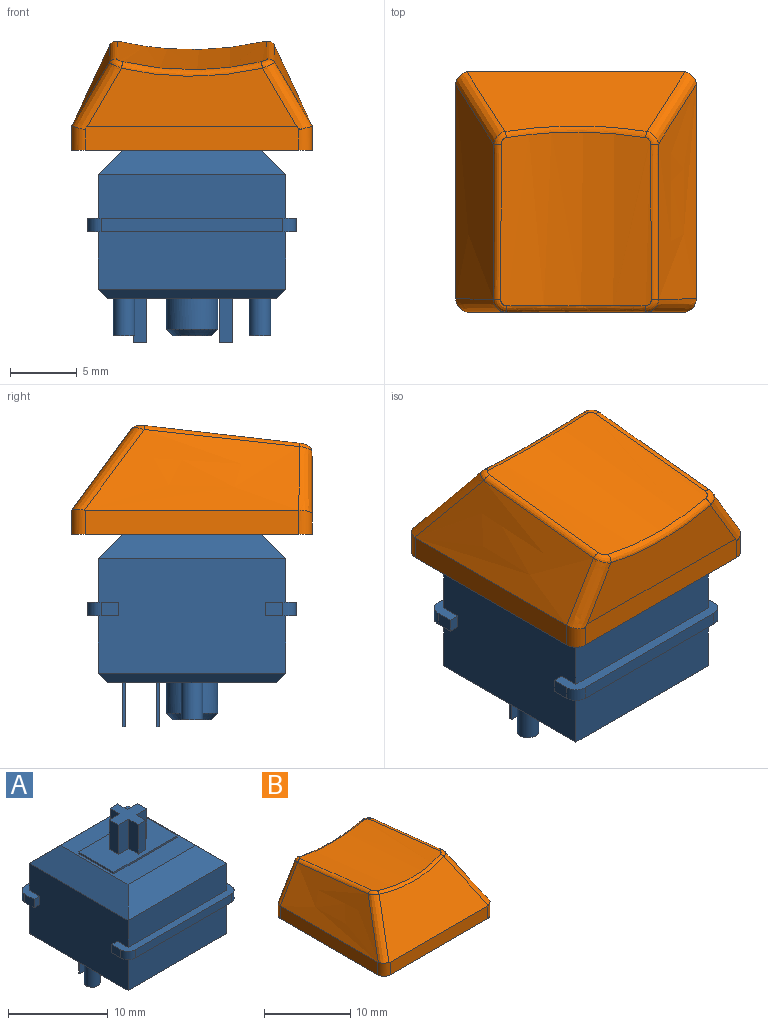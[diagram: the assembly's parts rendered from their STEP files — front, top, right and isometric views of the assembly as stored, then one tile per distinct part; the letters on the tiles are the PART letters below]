
ASSEMBLY  parts=2 mates=1
PART A: 69 faces, bbox 15.6x15.6x18.6 mm
  f0: plane 15.6x2.3mm, normal (0,0,-1), area 14.4mm2, adj f2,f3,f28,f30,f35,f60,f62,f63
  f1: plane 15.6x2.3mm, normal (0,0,-1), area 14.4mm2, adj f28,f30,f33,f34,f36,f59,f61,f64
  f2: plane 1.3x1mm, normal (1,0,0), area 1.3mm2, adj f0,f32,f62,f66
  f3: plane 1.3x1mm, normal (-1,0,0), area 1.3mm2, adj f0,f32,f63,f68
  f4: plane 15.6x2.3mm, normal (0,0,1), area 14.4mm2, adj f28,f30,f31,f33,f34,f36,f61,f64
  f5: plane 14x2.2mm, normal (-0.71,0,0.71), area 36.7mm2, adj f6,f7,f26,f30
  f6: plane 14x2.2mm, normal (0,-0.71,0.71), area 36.7mm2, adj f5,f7,f27,f31
  f7: plane 9.6x9.6mm, normal (0,0,1), area 47.2mm2, adj f5,f6,f8,f9,f10,f11,f26,f27
  f8: plane 5x0.2mm, normal (1,0,0), area 1mm2, adj f7,f9,f11,f12
  f9: plane 9x0.2mm, normal (0,1,0), area 1.8mm2, adj f7,f8,f10,f12
  f10: plane 5x0.2mm, normal (-1,0,0), area 1mm2, adj f7,f9,f11,f12
  f11: plane 9x0.2mm, normal (0,-1,0), area 1.8mm2, adj f7,f8,f10,f12
  f12: plane 9x5mm, normal (0,0,1), area 36.9mm2, adj f8,f9,f10,f11,f13,f14,f15,f16
  f13: plane 3.6x1.35mm, normal (1,0,0), area 4.9mm2, adj f12,f14,f24,f25
  f14: plane 3.6x1.08mm, normal (0,1,0), area 3.9mm2, adj f12,f13,f15,f25
  f15: plane 3.6x1.35mm, normal (-1,0,0), area 4.9mm2, adj f12,f14,f16,f25
  f16: plane 3.6x1.46mm, normal (0,1,0), area 5.3mm2, adj f12,f15,f17,f25
  f17: plane 3.6x1.3mm, normal (-1,0,0), area 4.7mm2, adj f12,f16,f18,f25
  f18: plane 3.6x1.46mm, normal (0,-1,0), area 5.3mm2, adj f12,f17,f19,f25
  f19: plane 3.6x1.35mm, normal (-1,0,0), area 4.9mm2, adj f12,f18,f20,f25
  f20: plane 3.6x1.08mm, normal (0,-1,0), area 3.9mm2, adj f12,f19,f21,f25
  f21: plane 3.6x1.35mm, normal (1,0,0), area 4.9mm2, adj f12,f20,f22,f25
  f22: plane 3.6x1.46mm, normal (0,-1,0), area 5.3mm2, adj f12,f21,f23,f25
  f23: plane 3.6x1.3mm, normal (1,0,0), area 4.7mm2, adj f12,f22,f24,f25
  f24: plane 3.6x1.46mm, normal (0,1,0), area 5.3mm2, adj f12,f13,f23,f25
  f25: plane 4x4mm, normal (0,0,1), area 8.1mm2, adj f13,f14,f15,f16,f17,f18,f19,f20
  f26: plane 14x2.2mm, normal (0,0.71,0.71), area 36.7mm2, adj f5,f7,f27,f29
  f27: plane 14x2.2mm, normal (0.71,0,0.71), area 36.7mm2, adj f6,f7,f26,f28
  f28: plane 14x8.6mm, normal (1,0,0), area 117.4mm2, adj f0,f1,f4,f27,f29,f31,f32,f55
  f29: plane 14x3.3mm, normal (0,1,0), area 46.2mm2, adj f26,f28,f30,f32
  f30: plane 14x8.6mm, normal (-1,0,0), area 117.4mm2, adj f0,f1,f4,f5,f29,f31,f32,f57
  f31: plane 14x3.3mm, normal (0,-1,0), area 46.2mm2, adj f4,f6,f28,f30
  f32: plane 15.6x2.3mm, normal (0,0,1), area 14.4mm2, adj f2,f3,f28,f29,f30,f35,f62,f63
  f33: plane 13.6x1mm, normal (0,-1,0), area 13.6mm2, adj f1,f4,f61,f64
  f34: plane 1.3x1mm, normal (1,0,0), area 1.3mm2, adj f1,f4,f61,f65
  f35: plane 13.6x1mm, normal (0,1,0), area 13.6mm2, adj f0,f32,f62,f63
  f36: plane 1.3x1mm, normal (-1,0,0), area 1.3mm2, adj f1,f4,f64,f67
  f37: plane 2.85x2.85mm, normal (0,0,-1), area 6.4mm2, adj f38
  f38: cone r=1.43mm half-angle=45deg, axis (0,0,1), area 7.4mm2, adj f37,f43
  f39: plane 1x0.2mm, normal (0,0,-1), area 0.2mm2, adj f44,f45,f46,f47
  f40: plane 1x0.2mm, normal (0,0,-1), area 0.2mm2, adj f48,f49,f50,f51
  f41: plane 1.6x1.6mm, normal (0,0,-1), area 2mm2, adj f52
  f42: plane 1.6x1.6mm, normal (0,0,-1), area 2mm2, adj f53
  f43: cylinder r=1.93mm len=3.85mm, axis (0,0,1), area 27.8mm2, adj f38,f54
  f44: plane 3.3x0.2mm, normal (-1,0,0), area 0.7mm2, adj f39,f45,f47,f54
  f45: plane 3.3x1mm, normal (0,1,0), area 3.3mm2, adj f39,f44,f46,f54
  f46: plane 3.3x0.2mm, normal (1,0,0), area 0.7mm2, adj f39,f45,f47,f54
  f47: plane 3.3x1mm, normal (0,-1,0), area 3.3mm2, adj f39,f44,f46,f54
  f48: plane 3.3x0.2mm, normal (-1,0,0), area 0.7mm2, adj f40,f49,f51,f54
  f49: plane 3.3x1mm, normal (0,1,0), area 3.3mm2, adj f40,f48,f50,f54
  f50: plane 3.3x0.2mm, normal (1,0,0), area 0.7mm2, adj f40,f49,f51,f54
  f51: plane 3.3x1mm, normal (0,-1,0), area 3.3mm2, adj f40,f48,f50,f54
  f52: cylinder r=0.8mm len=2.8mm, axis (0,0,1), area 14.1mm2, adj f41,f54
  f53: cylinder r=0.8mm len=2.8mm, axis (0,0,1), area 14.1mm2, adj f42,f54
  f54: plane 12.6x12.6mm, normal (0,0,-1), area 142.7mm2, adj f43,f44,f45,f46,f47,f48,f49,f50
  f55: plane 14x0.7mm, normal (0.71,0,-0.71), area 13.2mm2, adj f28,f54,f56,f58
  f56: plane 14x0.7mm, normal (0,0.71,-0.71), area 13.2mm2, adj f54,f55,f57,f60
  f57: plane 14x0.7mm, normal (-0.71,0,-0.71), area 13.2mm2, adj f30,f54,f56,f58
  f58: plane 14x0.7mm, normal (0,-0.71,-0.71), area 13.2mm2, adj f54,f55,f57,f59
  f59: plane 14x4.3mm, normal (0,-1,0), area 60.2mm2, adj f1,f28,f30,f58
  f60: plane 14x4.3mm, normal (0,1,0), area 60.2mm2, adj f0,f28,f30,f56
  f61: cylinder r=1mm len=1mm, axis (0,0,-1), area 1.6mm2, adj f1,f4,f33,f34
  f62: cylinder r=1mm len=1mm, axis (0,0,1), area 1.6mm2, adj f0,f2,f32,f35
  f63: cylinder r=1mm len=1mm, axis (0,0,-1), area 1.6mm2, adj f0,f3,f32,f35
  f64: cylinder r=1mm len=1mm, axis (0,0,1), area 1.6mm2, adj f1,f4,f33,f36
  f65: plane 1x0.8mm, normal (0,1,0), area 0.8mm2, adj f1,f4,f28,f34
  f66: plane 1x0.8mm, normal (0,-1,0), area 0.8mm2, adj f0,f2,f28,f32
  f67: plane 1x0.8mm, normal (0,1,0), area 0.8mm2, adj f1,f4,f30,f36
  f68: plane 1x0.8mm, normal (0,-1,0), area 0.8mm2, adj f0,f3,f30,f32
PART B: 50 faces, bbox 21.2x22.7x10.6 mm
  f0: plane 18x18mm, normal (0,0,-1), area 67.1mm2, adj f1,f2,f3,f4,f10,f12,f14,f16
  f1: plane 16x1.8mm, normal (1,0,0), area 28.8mm2, adj f0,f8,f10,f16
  f2: plane 16.02x1.82mm, normal (0,1,0), area 28.8mm2, adj f0,f5,f14,f15,f16,f17
  f3: plane 16x1.8mm, normal (-1,0,0), area 28.8mm2, adj f0,f6,f12,f14
  f4: plane 16x1.8mm, normal (0,-1,0), area 28.8mm2, adj f0,f7,f10,f12
  f5: plane 15.68x4.35mm, normal (0,1,0), area 52.7mm2, adj f2,f15,f17,f20
  f6: bspline ~18x6.51mm, area 85.6mm2, adj f3,f12,f13,f15,f19
  f7: plane 16.34x6.11mm, normal (0,-0.81,0.59), area 97.2mm2, adj f4,f10,f11,f12,f13,f23
  f8: bspline ~18x6.51mm, area 85.6mm2, adj f1,f10,f11,f17,f24
  f9: cylinder r=22.9mm len=13.02mm, axis (0,0.99,-0.11), area 145.8mm2, adj f18,f19,f20,f21,f22,f23,f24,f25
  f10: cylinder r=1mm len=1.88mm, axis (0,0,-1), area 2.9mm2, adj f0,f1,f4,f7,f8,f11
  f11: bspline ~8.07x6.49mm, area 10.8mm2, adj f7,f8,f10,f25
  f12: cylinder r=1mm len=1.88mm, axis (0,0,1), area 2.9mm2, adj f0,f3,f4,f6,f7,f13
  f13: bspline ~8.08x6.5mm, area 10.8mm2, adj f6,f7,f12,f21
  f14: cylinder r=1mm len=1.8mm, axis (0,0,-1), area 2.7mm2, adj f0,f2,f3,f15
  f15: bspline ~6.93x4.65mm, area 8.3mm2, adj f2,f5,f6,f14,f18
  f16: cylinder r=1mm len=1.8mm, axis (0,0,1), area 2.7mm2, adj f0,f1,f2,f17
  f17: bspline ~6.92x4.64mm, area 8.3mm2, adj f2,f5,f8,f16,f22
  f18: bspline ~1.17x1.07mm, area 0.8mm2, adj f9,f15,f19,f20
  f19: bspline ~17.39x2.3mm, area 7.9mm2, adj f6,f9,f18,f21
  f20: bspline ~10.57x1.09mm, area 7.6mm2, adj f5,f9,f18,f22
  f21: bspline ~1.3x1.11mm, area 0.6mm2, adj f9,f13,f19,f23
  f22: bspline ~1.23x1.01mm, area 0.8mm2, adj f9,f17,f20,f24
  f23: bspline ~10.63x0.88mm, area 5.6mm2, adj f7,f9,f21,f25
  f24: bspline ~17.39x2.3mm, area 7.9mm2, adj f8,f9,f22,f25
  f25: bspline ~1.3x1.11mm, area 0.6mm2, adj f9,f11,f23,f24
  f26: plane 16.04x1.61mm, normal (-1,0,0), area 24.9mm2, adj f0,f27,f29,f32,f33
  f27: plane 16x1.8mm, normal (0,-1,0), area 28.7mm2, adj f0,f26,f28,f30,f31,f33
  f28: plane 16.04x1.61mm, normal (1,0,0), area 24.9mm2, adj f0,f27,f29,f31,f32
  f29: plane 16x1.47mm, normal (0,1,0), area 23.6mm2, adj f0,f26,f28,f32
  f30: plane 15.83x4.1mm, normal (0,-1,0), area 47.9mm2, adj f27,f31,f33,f34
  f31: offset ~20x8.51mm, area 77.3mm2, adj f27,f28,f30,f32,f34
  f32: plane 16.71x6.33mm, normal (0,0.81,-0.59), area 88.7mm2, adj f26,f28,f29,f31,f33,f34
  f33: offset ~20x8.51mm, area 77.3mm2, adj f26,f27,f30,f32,f34
  f34: cylinder r=23.9mm len=11.93mm, axis (0,0.99,-0.11), area 107.8mm2, adj f30,f31,f32,f33,f46
  f35: plane 5.35x1.5mm, normal (-1,0,0), area 7.9mm2, adj f36,f44,f45,f49
  f36: plane 5.44x1.5mm, normal (0,-1,0), area 8.1mm2, adj f35,f37,f45,f49
  f37: plane 5.58x1.3mm, normal (-1,0,0), area 7.2mm2, adj f36,f38,f45,f49
  f38: plane 5.59x1.5mm, normal (0,1,0), area 8.3mm2, adj f37,f39,f45,f49
  f39: plane 5.67x1.5mm, normal (-1,0,0), area 8.4mm2, adj f38,f40,f45,f49
  f40: plane 5.67x1.3mm, normal (0,1,0), area 7.4mm2, adj f39,f41,f45,f49
  f41: plane 5.67x1.5mm, normal (1,0,0), area 8.4mm2, adj f40,f42,f45,f49
  f42: plane 5.59x1.5mm, normal (0,1,0), area 8.3mm2, adj f41,f43,f45,f49
  f43: plane 5.58x1.3mm, normal (1,0,0), area 7.2mm2, adj f42,f45,f47,f49
  f44: plane 5.17x1.3mm, normal (0,-1,0), area 6.7mm2, adj f35,f45,f48,f49
  f45: plane 5.5x5.5mm, normal (0,0,-1), area 14.3mm2, adj f35,f36,f37,f38,f39,f40,f41,f42
  f46: cylinder r=2.75mm len=5.57mm, axis (0,0,-1), area 96.3mm2, adj f34,f45
  f47: plane 5.44x1.5mm, normal (0,-1,0), area 8.1mm2, adj f43,f45,f48,f49
  f48: plane 5.35x1.5mm, normal (1,0,0), area 7.9mm2, adj f44,f45,f47,f49
  f49: cylinder r=23.9mm len=4.31mm, axis (0,0.99,-0.11), area 9.6mm2, adj f35,f36,f37,f38,f39,f40,f41,f42
PLACE A at identity fixed
PLACE B rot(axis=(0,0,1),180deg) t=(0,0,11.1)mm
MATE fastened A.f38 <-> B.f46  axis (0,0,1) through (0,0,11.7)mm
